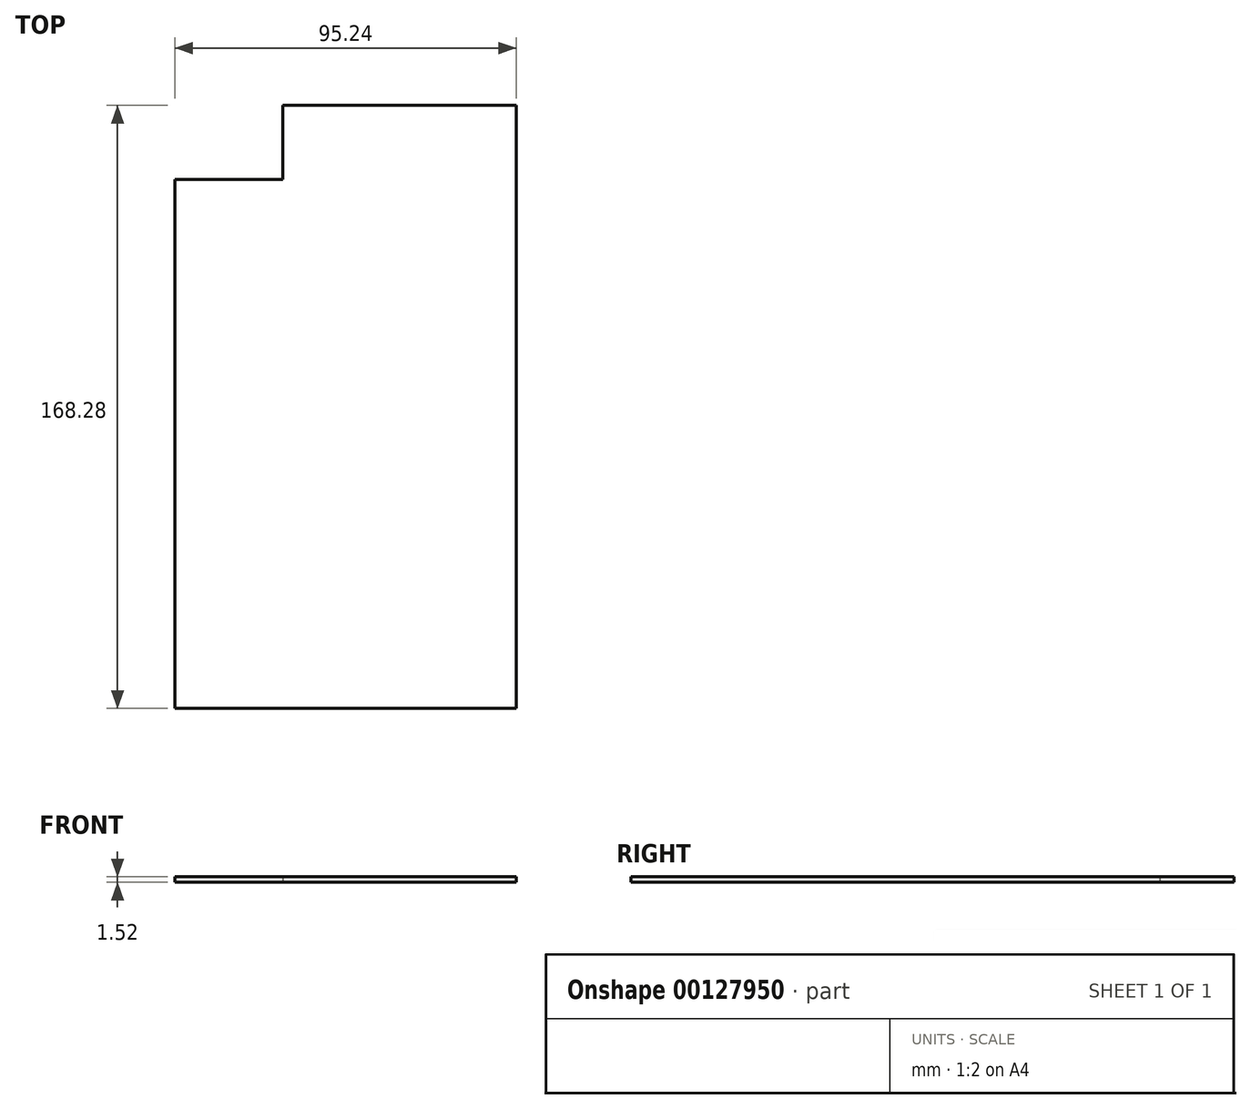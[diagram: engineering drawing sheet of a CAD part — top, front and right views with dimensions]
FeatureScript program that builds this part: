
annotation { "Feature Type Name" : "Feature", "Feature Type Description" : "" }
export const myFeature = defineFeature(function(context is Context, id is Id, definition is map)
    precondition{}
    {
        {
            var Q0;
            Q0=qCreatedBy(makeId("Top.planeOp"),FACE);
            var sketch = newSketch(context, id + "F0", { "sketchPlane" : qUnion([Q0])});
            skLineSegment(sketch, "E0.bottom", {"start": v(47.62, -84.14) * mm, "end": v(-47.63, -84.14) * mm});
            skLineSegment(sketch, "E0.top", {"start": v(47.63, 84.14) * mm, "end": v(-17.46, 84.14) * mm});
            skLineSegment(sketch, "E0.left", {"start": v(47.62, -84.14) * mm, "end": v(47.63, 84.14) * mm});
            skLineSegment(sketch, "E0.right", {"start": v(-47.63, -84.14) * mm, "end": v(-47.62, 63.5) * mm});
            skPoint(sketch, "E0.middle", {"position": v(0, 0) * mm});
            skLineSegment(sketch, "E1", {"start": v(-47.62, 63.5) * mm, "end": v(-17.46, 63.5) * mm});
            skLineSegment(sketch, "E2", {"start": v(-17.46, 63.5) * mm, "end": v(-17.46, 84.14) * mm});
            skPoint(sketch, "E3.orphan", {"position": v(-47.62, 84.14) * mm});
            skSolve(sketch);
        }
        {
            var Q0;
            Q0 = qSketchRegion(id + "F0", true);
            extrude(context, id + "F1", {"entities" : qUnion([Q0]), "depth" : 1.52 * mm});
        }
    });
